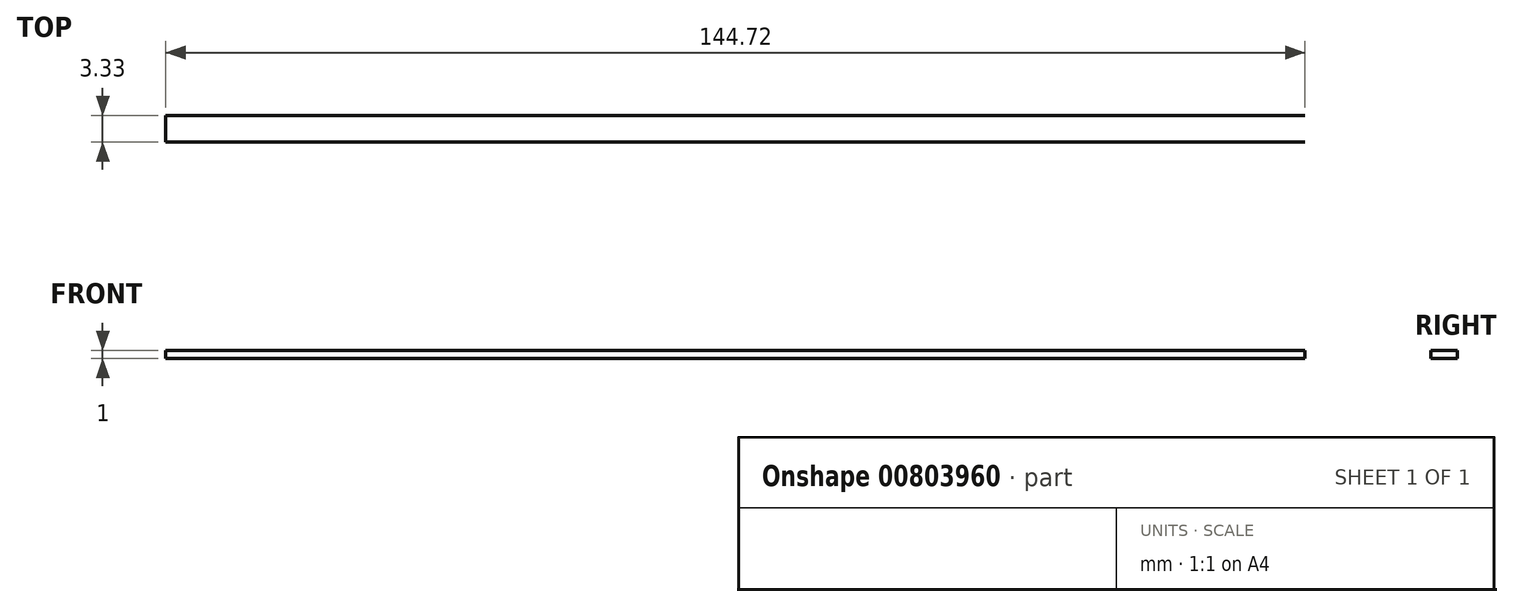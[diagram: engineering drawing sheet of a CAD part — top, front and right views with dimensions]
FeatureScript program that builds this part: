
annotation { "Feature Type Name" : "Feature", "Feature Type Description" : "" }
export const myFeature = defineFeature(function(context is Context, id is Id, definition is map)
    precondition{}
    {
        {
            var Q0;
            Q0=qCreatedBy(makeId("Top.planeOp"),FACE);
            var sketch = newSketch(context, id + "F0", { "sketchPlane" : qUnion([Q0])});
            skLineSegment(sketch, "E0.bottom", {"start": v(-105.17, -20.49) * mm, "end": v(39.55, -20.49) * mm});
            skLineSegment(sketch, "E0.top", {"start": v(-105.17, -23.82) * mm, "end": v(39.55, -23.82) * mm});
            skLineSegment(sketch, "E0.left", {"start": v(-105.17, -20.49) * mm, "end": v(-105.17, -23.82) * mm});
            skLineSegment(sketch, "E0.right", {"start": v(39.55, -20.49) * mm, "end": v(39.55, -23.82) * mm});
            skSolve(sketch);
        }
        {
            var Q0;
            Q0 = qSketchRegion(id + "F0", true);
            var Q1;
            Q1=sQuery(id+"F0.wireOp",EDGE,"E0.top");
            var Q2;
            Q2=sQuery(id+"F0.wireOp",EDGE,"E0.left");
            var Q3;
            Q3=sQuery(id+"F0.wireOp",EDGE,"E0.bottom");
            extrude(context, id + "F1", {"entities" : qUnion([Q0]), "bodyType" : ToolBodyType.SURFACE, "surfaceEntities" : qUnion([Q1, Q2, Q3]), "depth" : 1 * mm, "offsetDistance" : 25.4 * mm});
        }
    });
